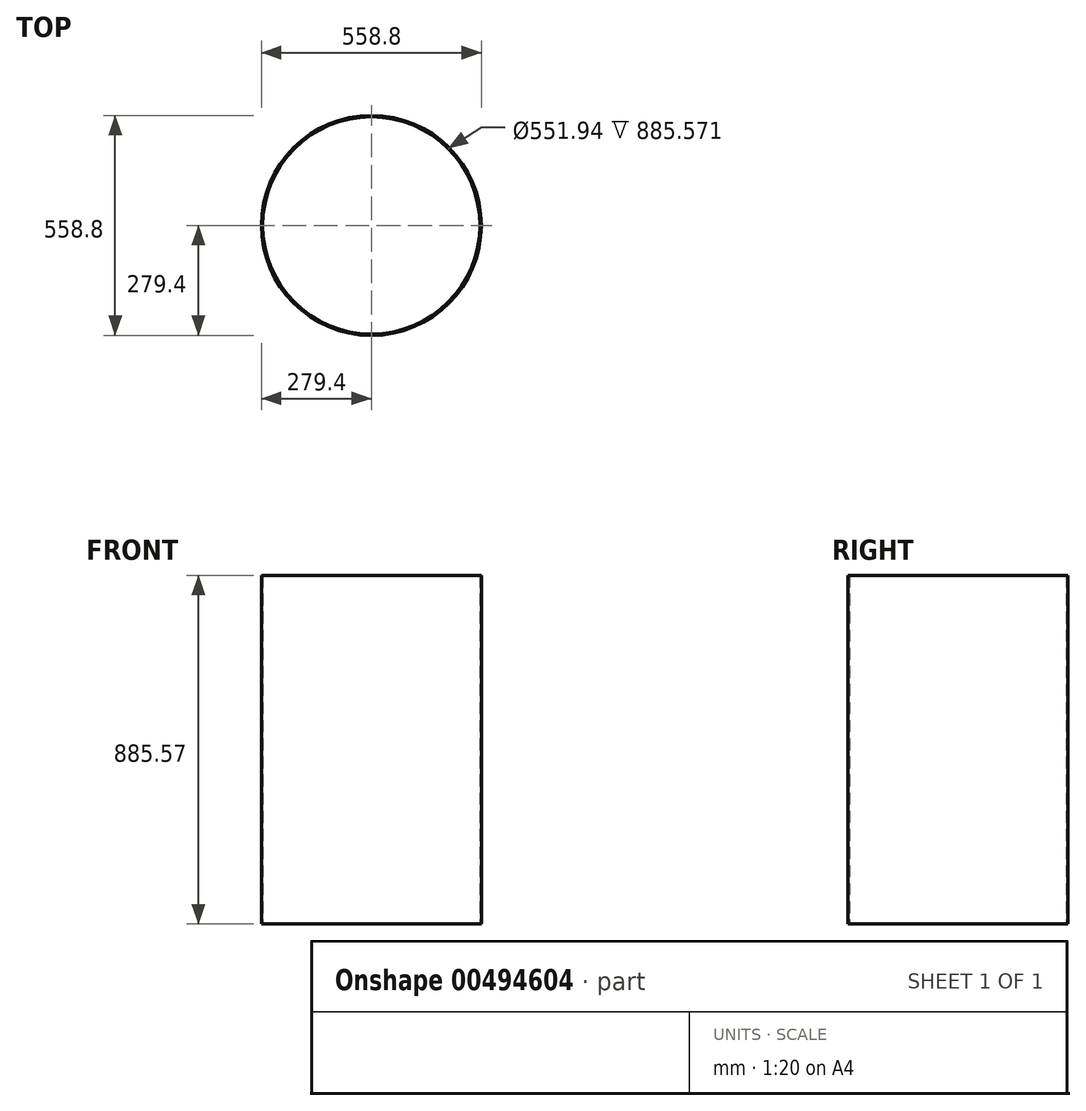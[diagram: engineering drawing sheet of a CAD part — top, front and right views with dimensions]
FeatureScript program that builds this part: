
annotation { "Feature Type Name" : "Feature", "Feature Type Description" : "" }
export const myFeature = defineFeature(function(context is Context, id is Id, definition is map)
    precondition{}
    {
        {
            var Q0;
            Q0=qCreatedBy(makeId("Top.planeOp"),FACE);
            var sketch = newSketch(context, id + "F0", { "sketchPlane" : qUnion([Q0])});
            skCircle(sketch, "E0", {"center": v(0, 0) * mm, "radius": 279.4 * mm});
            skCircle(sketch, "E1.0", {"center": v(0, 0) * mm, "radius": 275.97 * mm});
            skSolve(sketch);
        }
        {
            var Q0;
            Q0=qSketchRegion(id+"F0",true);
            extrude(context, id + "F1", {"entities" : qUnion([Q0]), "depth" : 885.57 * mm, "offsetDistance" : 25.4 * mm});
        }
    });
